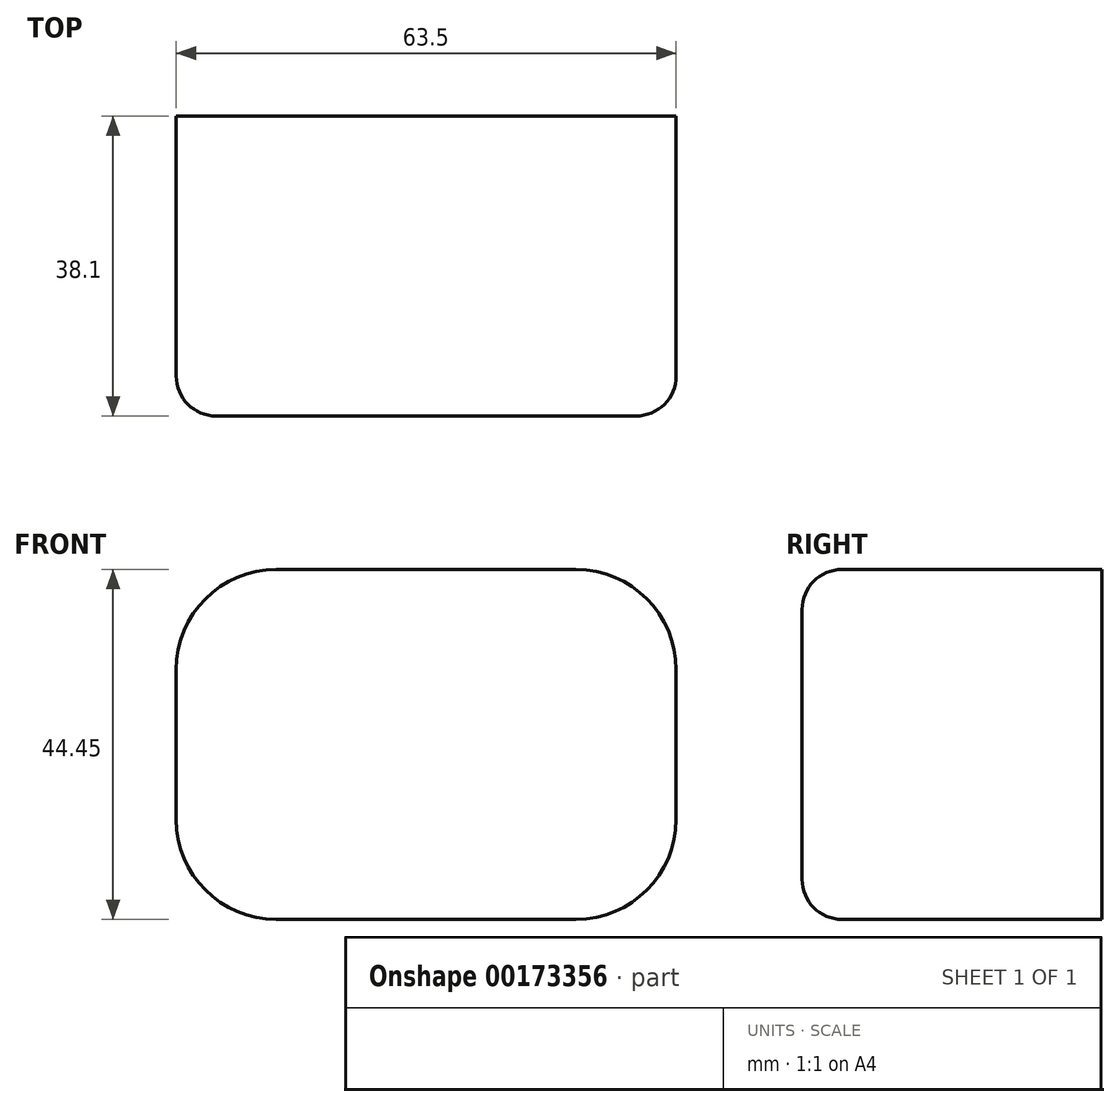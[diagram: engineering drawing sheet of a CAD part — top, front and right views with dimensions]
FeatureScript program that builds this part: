
annotation { "Feature Type Name" : "Feature", "Feature Type Description" : "" }
export const myFeature = defineFeature(function(context is Context, id is Id, definition is map)
    precondition{}
    {
        {
            var Q0;
            Q0=qCreatedBy(makeId("Front.planeOp"),FACE);
            var sketch = newSketch(context, id + "F0", { "sketchPlane" : qUnion([Q0])});
            skLineSegment(sketch, "E0.bottom", {"start": v(0, 0) * mm, "end": v(63.5, 0) * mm});
            skLineSegment(sketch, "E0.top", {"start": v(0, 44.45) * mm, "end": v(63.5, 44.45) * mm});
            skLineSegment(sketch, "E0.left", {"start": v(0, 0) * mm, "end": v(0, 44.45) * mm});
            skLineSegment(sketch, "E0.right", {"start": v(63.5, 0) * mm, "end": v(63.5, 44.45) * mm});
            skSolve(sketch);
        }
        {
            var Q0;
            Q0 = qSketchRegion(id + "F0", true);
            extrude(context, id + "F1", {"entities" : qUnion([Q0]), "depth" : 12.7 * mm});
        }
        {
            var Q0;
            Q0=makeQuery(id+"F1.opExtrude","SWEPT_EDGE",EDGE,{"disambiguationData":[OSD([sQuery(id+"F0.wireOp",EDGE,"E0.top"),sQuery(id+"F0.wireOp",EDGE,"E0.left")])]});
            fillet(context, id + "F2", {"entities" : qUnion([Q0]), "radius" : 12.7 * mm, "tangentPropagation" : true, "allowEdgeOverflow" : false});
        }
        {
            var Q0;
            Q0=makeQuery(id+"F1.opExtrude","SWEPT_EDGE",EDGE,{"disambiguationData":[OSD([sQuery(id+"F0.wireOp",EDGE,"E0.top"),sQuery(id+"F0.wireOp",EDGE,"E0.right")])]});
            fillet(context, id + "F3", {"entities" : qUnion([Q0]), "radius" : 12.7 * mm, "tangentPropagation" : true, "allowEdgeOverflow" : false});
        }
        {
            var Q0;
            Q0=makeQuery(id+"F1.opExtrude","SWEPT_EDGE",EDGE,{"disambiguationData":[OSD([sQuery(id+"F0.wireOp",EDGE,"E0.bottom"),sQuery(id+"F0.wireOp",EDGE,"E0.left")])]});
            fillet(context, id + "F4", {"entities" : qUnion([Q0]), "radius" : 12.7 * mm, "tangentPropagation" : true, "allowEdgeOverflow" : false});
        }
        {
            var Q0;
            Q0=makeQuery(id+"F1.opExtrude","SWEPT_EDGE",EDGE,{"disambiguationData":[OSD([sQuery(id+"F0.wireOp",EDGE,"E0.bottom"),sQuery(id+"F0.wireOp",EDGE,"E0.right")])]});
            fillet(context, id + "F5", {"entities" : qUnion([Q0]), "radius" : 12.7 * mm, "tangentPropagation" : true, "allowEdgeOverflow" : false});
        }
        {
            var Q0;
            {var subQ0=sQuery(id+"F0.wireOp",EDGE,"E0.right");var subQ1=sQuery(id+"F0.wireOp",EDGE,"E0.top");Q0=makeQuery(id+"F3.opFillet","BLEND_EDGE",EDGE,{"blendedFrom":[makeQuery(id+"F1.opExtrude","SWEPT_EDGE",EDGE,{"disambiguationData":[OSD([subQ1,subQ0])]}),makeQuery(id+"F1.opExtrude","CAP_FACE",FACE,{"disambiguationData":[OSD([sQuery(id+"F0.wireOp",EDGE,"E0.bottom"),subQ1,sQuery(id+"F0.wireOp",EDGE,"E0.left"),subQ0])],"isStart":false})],"blendedInto":[makeQuery(id+"F1.opExtrude","CAP_FACE",FACE,{"disambiguationData":[OSD([sQuery(id+"F0.wireOp",EDGE,"E0.bottom"),subQ1,sQuery(id+"F0.wireOp",EDGE,"E0.left"),subQ0])],"isStart":false})]});}
            fillet(context, id + "F6", {"entities" : qUnion([Q0]), "radius" : 5.08 * mm, "tangentPropagation" : true, "allowEdgeOverflow" : false});
        }
        {
            var Q0;
            Q0=makeQuery(id+"F1.opExtrude","CAP_FACE",FACE,{"disambiguationData":[OSD([sQuery(id+"F0.wireOp",EDGE,"E0.bottom"),sQuery(id+"F0.wireOp",EDGE,"E0.top"),sQuery(id+"F0.wireOp",EDGE,"E0.left"),sQuery(id+"F0.wireOp",EDGE,"E0.right")])],"isStart":true});
            extrude(context, id + "F7", {"entities" : qUnion([Q0]), "operationType" : NewBodyOperationType.ADD, "depth" : 25.4 * mm});
        }
    });
